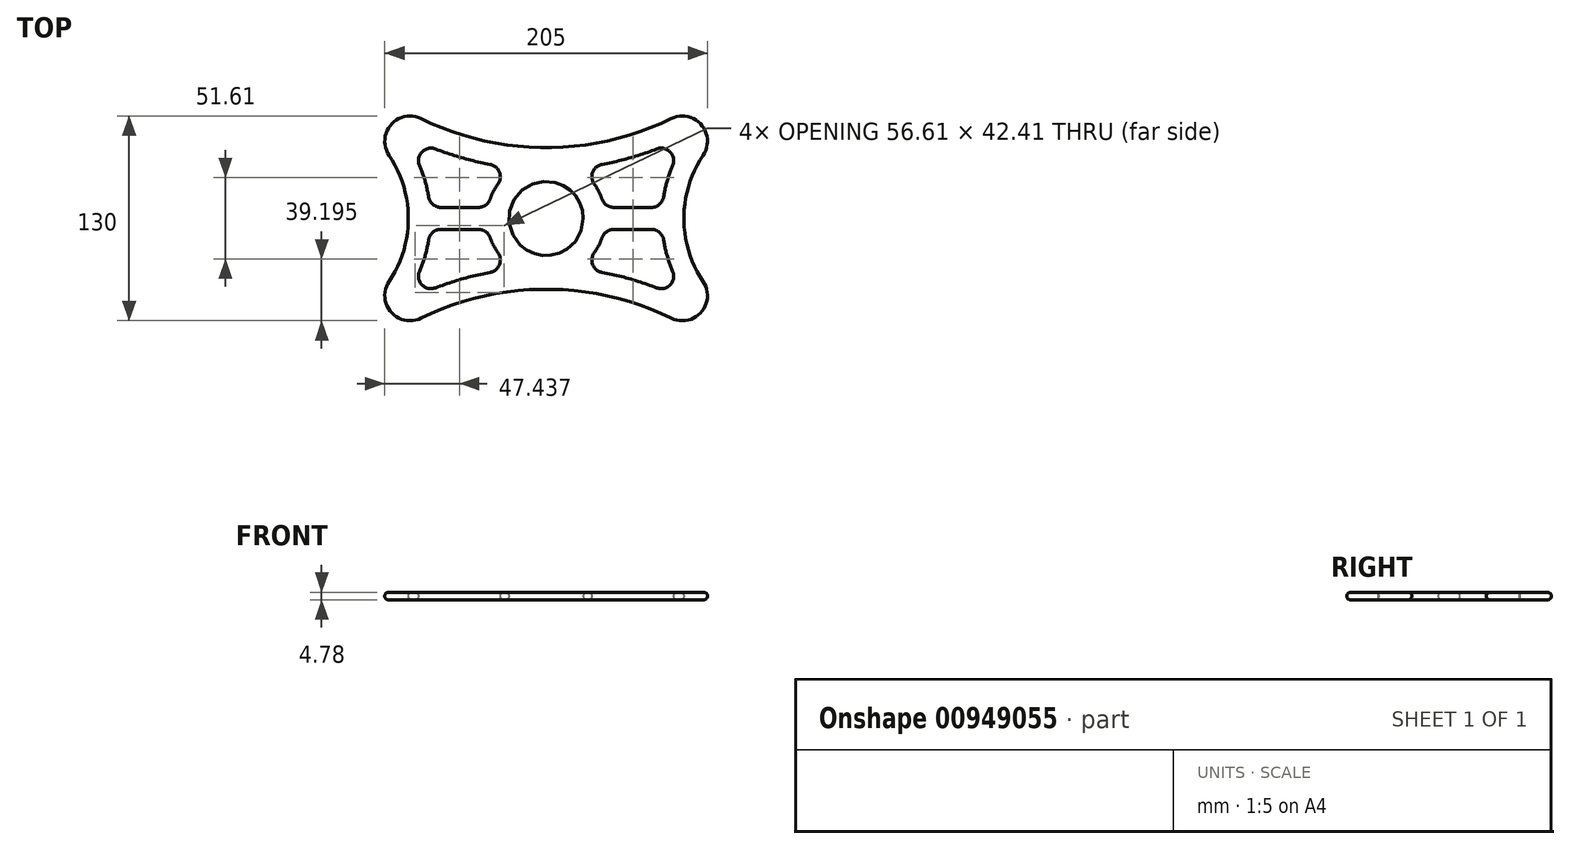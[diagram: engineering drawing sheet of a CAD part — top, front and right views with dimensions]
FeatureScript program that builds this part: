
annotation { "Feature Type Name" : "Feature", "Feature Type Description" : "" }
export const myFeature = defineFeature(function(context is Context, id is Id, definition is map)
    precondition{}
    {
        {
            var Q0;
            Q0=qCreatedBy(makeId("Top.planeOp"),FACE);
            var sketch = newSketch(context, id + "F0", { "sketchPlane" : qUnion([Q0])});
            skLineSegment(sketch, "E0.bottom", {"start": v(-102.5, 65) * mm, "end": v(102.5, 65) * mm, "construction": true});
            skLineSegment(sketch, "E0.top", {"start": v(-102.5, -65) * mm, "end": v(102.5, -65) * mm, "construction": true});
            skLineSegment(sketch, "E0.left", {"start": v(-102.5, 65) * mm, "end": v(-102.5, -65) * mm, "construction": true});
            skLineSegment(sketch, "E0.right", {"start": v(102.5, 65) * mm, "end": v(102.5, -65) * mm, "construction": true});
            skPoint(sketch, "E0.middle", {"position": v(0, 0) * mm});
            skArc(sketch, "E1", {"start": v(-79.48, 63.38) * mm, "mid": v(-98.58, 59.5) * mm, "end": v(-99.76, 40.04) * mm});
            skArc(sketch, "E2.MirrorC", {"start": v(79.48, 63.38) * mm, "mid": v(98.58, 59.5) * mm, "end": v(99.76, 40.04) * mm});
            skArc(sketch, "E3.MirrorC", {"start": v(79.48, -63.38) * mm, "mid": v(98.58, -59.5) * mm, "end": v(99.76, -40.04) * mm});
            skArc(sketch, "E4.MirrorC", {"start": v(-79.48, -63.38) * mm, "mid": v(-98.58, -59.5) * mm, "end": v(-99.76, -40.04) * mm});
            skLineSegment(sketch, "E5", {"start": v(0, 0) * mm, "end": v(0, 0) * mm});
            skPoint(sketch, "E5.endSnap0", {"position": v(0, 65) * mm});
            skLineSegment(sketch, "E6", {"start": v(0, 0) * mm, "end": v(0, -420.15) * mm, "construction": true});
            skPoint(sketch, "E7.endSnap0", {"position": v(102.5, 0) * mm});
            skLineSegment(sketch, "E8", {"start": v(0, 0) * mm, "end": v(-430.2, 0) * mm, "construction": true});
            skPoint(sketch, "E9", {"position": v(0, 45) * mm});
            skPoint(sketch, "E10", {"position": v(0, -45) * mm});
            skArc(sketch, "E11", {"start": v(-79.48, 63.38) * mm, "mid": v(0, 45) * mm, "end": v(79.48, 63.38) * mm});
            skArc(sketch, "E12.MirrorC", {"start": v(-79.48, -63.38) * mm, "mid": v(0, -45) * mm, "end": v(79.48, -63.38) * mm});
            skArc(sketch, "E13", {"start": v(99.76, 40.04) * mm, "mid": v(87.5, 0) * mm, "end": v(99.76, -40.04) * mm});
            skArc(sketch, "E14.MirrorC", {"start": v(-99.76, 40.04) * mm, "mid": v(-87.5, 0) * mm, "end": v(-99.76, -40.04) * mm});
            skCircle(sketch, "E15", {"center": v(0, 0) * mm, "radius": 23.6 * mm});
            skArc(sketch, "E16.0", {"start": v(-35.5, -12.32) * mm, "mid": v(-33.37, -17.28) * mm, "end": v(-30.55, -21.87) * mm});
            skArc(sketch, "E17.1", {"start": v(-80.4, 33.6) * mm, "mid": v(-76.9, 23.8) * mm, "end": v(-74.63, 13.65) * mm});
            skArc(sketch, "E17.2", {"start": v(-70.25, 44.12) * mm, "mid": v(-53.13, 38.4) * mm, "end": v(-35.56, 34.3) * mm});
            skArc(sketch, "E17.5", {"start": v(80.4, 33.6) * mm, "mid": v(76.9, 23.8) * mm, "end": v(74.63, 13.65) * mm});
            skArc(sketch, "E17.7", {"start": v(-70.25, -44.12) * mm, "mid": v(-53.13, -38.4) * mm, "end": v(-35.56, -34.3) * mm});
            skPoint(sketch, "E18", {"position": v(-87.5, 0) * mm});
            skLineSegment(sketch, "E19.top", {"start": v(-66.8, -6.99) * mm, "end": v(-43, -6.99) * mm});
            skLineSegment(sketch, "E20.bottom", {"start": v(43, 6.98) * mm, "end": v(66.8, 6.98) * mm});
            skLineSegment(sketch, "E20.top", {"start": v(43, -6.99) * mm, "end": v(66.8, -6.99) * mm});
            skLineSegment(sketch, "E21.trimOffspring", {"start": v(-66.8, 6.99) * mm, "end": v(-43, 6.99) * mm});
            skArc(sketch, "E22.trimOffspring", {"start": v(-74.63, -13.65) * mm, "mid": v(-76.9, -23.8) * mm, "end": v(-80.4, -33.6) * mm});
            skArc(sketch, "E23.trimOffspring", {"start": v(35.5, 12.32) * mm, "mid": v(33.37, 17.28) * mm, "end": v(30.55, 21.87) * mm});
            skArc(sketch, "E24.trimOffspring", {"start": v(35.56, 34.3) * mm, "mid": v(53.13, 38.4) * mm, "end": v(70.25, 44.12) * mm});
            skArc(sketch, "E25.trimOffspring", {"start": v(74.63, -13.65) * mm, "mid": v(76.9, -23.8) * mm, "end": v(80.4, -33.6) * mm});
            skArc(sketch, "E26.trimOffspring", {"start": v(-30.55, 21.87) * mm, "mid": v(-33.37, 17.28) * mm, "end": v(-35.5, 12.32) * mm});
            skArc(sketch, "E27.trimOffspring", {"start": v(30.55, -21.87) * mm, "mid": v(33.37, -17.28) * mm, "end": v(35.5, -12.32) * mm});
            skArc(sketch, "E28.trimOffspring", {"start": v(35.56, -34.3) * mm, "mid": v(53.13, -38.4) * mm, "end": v(70.25, -44.12) * mm});
            skPoint(sketch, "E29.visualSharp", {"position": v(-73.82, 6.99) * mm});
            skArc(sketch, "E29.filletArc", {"start": v(-74.63, 13.65) * mm, "mid": v(-71.94, 8.88) * mm, "end": v(-66.8, 6.99) * mm});
            skPoint(sketch, "E30.visualSharp", {"position": v(-36.92, 6.98) * mm});
            skArc(sketch, "E30.filletArc", {"start": v(-43, 6.99) * mm, "mid": v(-38.4, 8.45) * mm, "end": v(-35.5, 12.32) * mm});
            skPoint(sketch, "E31.visualSharp", {"position": v(-19.66, 32.02) * mm});
            skArc(sketch, "E31.filletArc", {"start": v(-30.55, 21.87) * mm, "mid": v(-29.65, 29.46) * mm, "end": v(-35.56, 34.3) * mm});
            skArc(sketch, "E32.filletArc", {"start": v(-70.25, 44.12) * mm, "mid": v(-78.82, 42.23) * mm, "end": v(-80.4, 33.6) * mm});
            skPoint(sketch, "E33.visualSharp", {"position": v(-73.82, -6.99) * mm});
            skArc(sketch, "E33.filletArc", {"start": v(-66.8, -6.99) * mm, "mid": v(-71.94, -8.88) * mm, "end": v(-74.63, -13.65) * mm});
            skArc(sketch, "E34.filletArc", {"start": v(-80.4, -33.6) * mm, "mid": v(-78.82, -42.23) * mm, "end": v(-70.25, -44.12) * mm});
            skPoint(sketch, "E35.visualSharp", {"position": v(-19.66, -32.02) * mm});
            skArc(sketch, "E35.filletArc", {"start": v(-35.56, -34.3) * mm, "mid": v(-29.65, -29.46) * mm, "end": v(-30.55, -21.87) * mm});
            skPoint(sketch, "E36.visualSharp", {"position": v(-36.92, -6.99) * mm});
            skArc(sketch, "E36.filletArc", {"start": v(-35.5, -12.32) * mm, "mid": v(-38.4, -8.45) * mm, "end": v(-43, -6.99) * mm});
            skPoint(sketch, "E37.visualSharp", {"position": v(19.66, 32.02) * mm});
            skArc(sketch, "E37.filletArc", {"start": v(35.56, 34.3) * mm, "mid": v(29.65, 29.46) * mm, "end": v(30.55, 21.87) * mm});
            skArc(sketch, "E38.filletArc", {"start": v(80.4, 33.6) * mm, "mid": v(78.82, 42.23) * mm, "end": v(70.25, 44.12) * mm});
            skPoint(sketch, "E39.visualSharp", {"position": v(73.82, 6.98) * mm});
            skArc(sketch, "E39.filletArc", {"start": v(66.8, 6.98) * mm, "mid": v(71.94, 8.88) * mm, "end": v(74.63, 13.65) * mm});
            skPoint(sketch, "E40.visualSharp", {"position": v(36.92, 6.98) * mm});
            skArc(sketch, "E40.filletArc", {"start": v(35.5, 12.32) * mm, "mid": v(38.4, 8.45) * mm, "end": v(43, 6.98) * mm});
            skPoint(sketch, "E41.visualSharp", {"position": v(36.92, -6.99) * mm});
            skArc(sketch, "E41.filletArc", {"start": v(43, -6.99) * mm, "mid": v(38.4, -8.45) * mm, "end": v(35.5, -12.32) * mm});
            skPoint(sketch, "E42.visualSharp", {"position": v(73.82, -6.99) * mm});
            skArc(sketch, "E42.filletArc", {"start": v(74.63, -13.65) * mm, "mid": v(71.94, -8.88) * mm, "end": v(66.8, -6.99) * mm});
            skPoint(sketch, "E43.visualSharp", {"position": v(19.66, -32.02) * mm});
            skArc(sketch, "E43.filletArc", {"start": v(30.55, -21.87) * mm, "mid": v(29.65, -29.46) * mm, "end": v(35.56, -34.3) * mm});
            skArc(sketch, "E44.filletArc", {"start": v(70.25, -44.12) * mm, "mid": v(78.82, -42.23) * mm, "end": v(80.4, -33.6) * mm});
            skSolve(sketch);
        }
        {
            var Q0;
            Q0=makeQuery(id+"F0.imprint","IMPRINT",FACE,{"disambiguationData":[TD([[makeQuery(id+"F0.imprint","IMPRINT",EDGE,{"derivedFrom":sQuery(id+"F0.wireOp",EDGE,"E1")}),1.0]])]});
            extrude(context, id + "F1", {"entities" : qUnion([Q0]), "depth" : 4.78 * mm, "offsetDistance" : 25.4 * mm});
        }
        {
            var Q0;
            Q0=makeQuery(id+"F1.opExtrude","CAP_EDGE",EDGE,{"disambiguationData":[OSD([sQuery(id+"F0.wireOp",EDGE,"E17.1")])],"isStart":false});
            var Q1;
            Q1=makeQuery(id+"F1.opExtrude","CAP_EDGE",EDGE,{"disambiguationData":[OSD([sQuery(id+"F0.wireOp",EDGE,"E37.filletArc")])],"isStart":false});
            var Q2;
            Q2=makeQuery(id+"F1.opExtrude","CAP_EDGE",EDGE,{"disambiguationData":[OSD([sQuery(id+"F0.wireOp",EDGE,"E27.trimOffspring")])],"isStart":false});
            var Q3;
            Q3=makeQuery(id+"F1.opExtrude","CAP_EDGE",EDGE,{"disambiguationData":[OSD([sQuery(id+"F0.wireOp",EDGE,"E22.trimOffspring")])],"isStart":false});
            var Q4;
            Q4=makeQuery(id+"F1.opExtrude","CAP_EDGE",EDGE,{"disambiguationData":[OSD([sQuery(id+"F0.wireOp",EDGE,"E15")])],"isStart":false});
            var Q5;
            Q5=makeQuery(id+"F1.opExtrude","CAP_EDGE",EDGE,{"disambiguationData":[OSD([sQuery(id+"F0.wireOp",EDGE,"E11")])],"isStart":false});
            var Q6;
            Q6=makeQuery(id+"F1.opExtrude","CAP_EDGE",EDGE,{"disambiguationData":[OSD([sQuery(id+"F0.wireOp",EDGE,"E12.MirrorC")])],"isStart":true});
            var Q7;
            Q7=makeQuery(id+"F1.opExtrude","CAP_EDGE",EDGE,{"disambiguationData":[OSD([sQuery(id+"F0.wireOp",EDGE,"E25.trimOffspring")])],"isStart":true});
            var Q8;
            Q8=makeQuery(id+"F1.opExtrude","CAP_EDGE",EDGE,{"disambiguationData":[OSD([sQuery(id+"F0.wireOp",EDGE,"E17.5")])],"isStart":true});
            var Q9;
            Q9=makeQuery(id+"F1.opExtrude","CAP_EDGE",EDGE,{"disambiguationData":[OSD([sQuery(id+"F0.wireOp",EDGE,"E15")])],"isStart":true});
            var Q10;
            Q10=makeQuery(id+"F1.opExtrude","CAP_EDGE",EDGE,{"disambiguationData":[OSD([sQuery(id+"F0.wireOp",EDGE,"E26.trimOffspring")])],"isStart":true});
            var Q11;
            Q11=makeQuery(id+"F1.opExtrude","CAP_EDGE",EDGE,{"disambiguationData":[OSD([sQuery(id+"F0.wireOp",EDGE,"E16.0")])],"isStart":true});
            fillet(context, id + "F2", {"entities" : qUnion([Q0, Q1, Q2, Q3, Q4, Q5, Q6, Q7, Q8, Q9, Q10, Q11]), "radius" : 2.4 * mm, "tangentPropagation" : true, "allowEdgeOverflow" : false});
        }
    });
